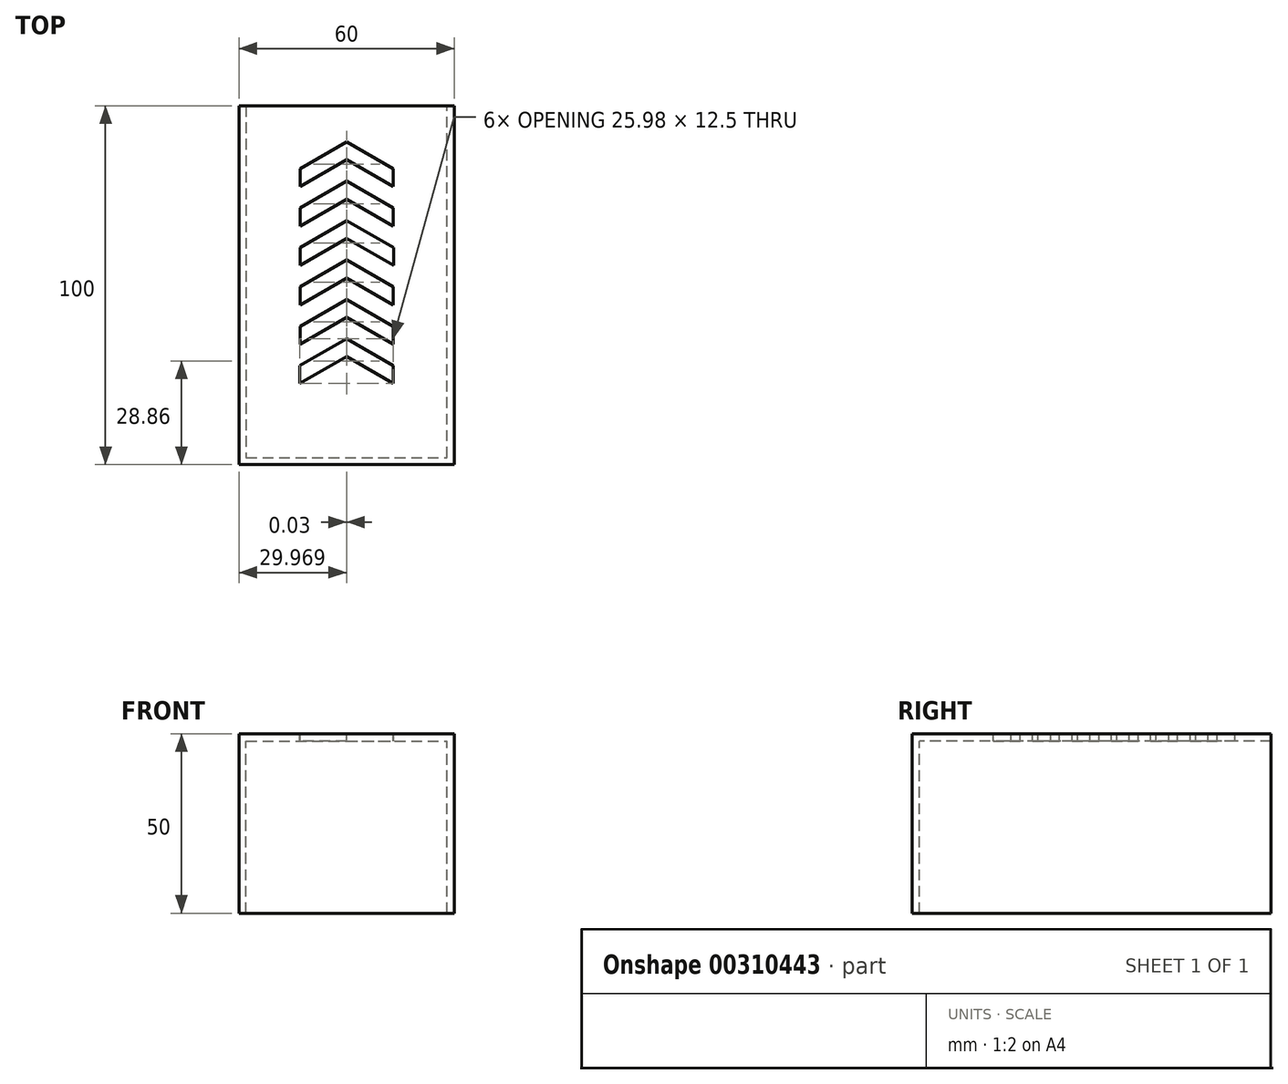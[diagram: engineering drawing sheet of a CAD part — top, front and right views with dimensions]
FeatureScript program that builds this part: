
annotation { "Feature Type Name" : "Feature", "Feature Type Description" : "" }
export const myFeature = defineFeature(function(context is Context, id is Id, definition is map)
    precondition{}
    {
        {
            var Q0;
            Q0=qCreatedBy(makeId("Top.planeOp"),FACE);
            var sketch = newSketch(context, id + "F0", { "sketchPlane" : qUnion([Q0])});
            skLineSegment(sketch, "E0", {"start": v(0, 0) * mm, "end": v(-30, 0) * mm});
            skLineSegment(sketch, "E1", {"start": v(-30, 0) * mm, "end": v(-30, -100) * mm});
            skLineSegment(sketch, "E2", {"start": v(-30, -100) * mm, "end": v(30, -100) * mm});
            skLineSegment(sketch, "E3", {"start": v(30, -100) * mm, "end": v(30, 0) * mm});
            skLineSegment(sketch, "E4", {"start": v(30, 0) * mm, "end": v(0, 0) * mm});
            skSolve(sketch);
        }
        {
            var Q0;
            Q0=makeQuery(id+"F0.imprint","IMPRINT",FACE,{"disambiguationData":[TD([[makeQuery(id+"F0.imprint","IMPRINT",EDGE,{"derivedFrom":sQuery(id+"F0.wireOp",EDGE,"E0")}),1.0]])]});
            extrude(context, id + "F1", {"entities" : qUnion([Q0]), "oppositeDirection" : true, "depth" : 50 * mm});
        }
        {
            var Q0;
            Q0=makeQuery(id+"F1.opExtrude","CAP_FACE",FACE,{"disambiguationData":[OSD([sQuery(id+"F0.wireOp",EDGE,"E0"),sQuery(id+"F0.wireOp",EDGE,"E1"),sQuery(id+"F0.wireOp",EDGE,"E2"),sQuery(id+"F0.wireOp",EDGE,"E3"),sQuery(id+"F0.wireOp",EDGE,"E4")])],"isStart":false});
            shell(context, id + "F2", {"entities" : qUnion([Q0]), "thickness" : 2 * mm});
        }
        {
            var Q0;
            Q0=makeQuery(id+"F1.opExtrude","CAP_FACE",FACE,{"disambiguationData":[OSD([sQuery(id+"F0.wireOp",EDGE,"E0"),sQuery(id+"F0.wireOp",EDGE,"E1"),sQuery(id+"F0.wireOp",EDGE,"E2"),sQuery(id+"F0.wireOp",EDGE,"E3"),sQuery(id+"F0.wireOp",EDGE,"E4")])],"isStart":true});
            var sketch = newSketch(context, id + "F3", { "sketchPlane" : qUnion([Q0])});
            skLineSegment(sketch, "E5", {"start": v(0, 0) * mm, "end": v(0, -10) * mm});
            skLineSegment(sketch, "E6", {"start": v(0, -10) * mm, "end": v(-13, -17.5) * mm});
            skLineSegment(sketch, "E7", {"start": v(-13, -17.5) * mm, "end": v(-13, -22.5) * mm});
            skLineSegment(sketch, "E8", {"start": v(-13, -22.5) * mm, "end": v(0, -15) * mm});
            skLineSegment(sketch, "E9", {"start": v(0, -10) * mm, "end": v(13, -17.5) * mm});
            skLineSegment(sketch, "E10", {"start": v(13, -17.5) * mm, "end": v(13, -22.5) * mm});
            skLineSegment(sketch, "E11", {"start": v(0, -15) * mm, "end": v(13, -22.5) * mm});
            skLineSegment(sketch, "E12", {"start": v(0, -15) * mm, "end": v(0, -21) * mm});
            skLineSegment(sketch, "E13", {"start": v(0, -21) * mm, "end": v(-13, -28.5) * mm});
            skLineSegment(sketch, "E14", {"start": v(-13, -28.5) * mm, "end": v(-13, -33.5) * mm});
            skLineSegment(sketch, "E15", {"start": v(-13, -33.5) * mm, "end": v(0, -26) * mm});
            skLineSegment(sketch, "E16", {"start": v(0, -21) * mm, "end": v(13, -28.5) * mm});
            skLineSegment(sketch, "E17", {"start": v(13, -28.5) * mm, "end": v(13, -33.5) * mm});
            skLineSegment(sketch, "E18", {"start": v(0, -26) * mm, "end": v(13, -33.5) * mm});
            skLineSegment(sketch, "E19", {"start": v(0, -26) * mm, "end": v(0, -32) * mm});
            skLineSegment(sketch, "E20.1.0.0", {"start": v(0.06, -31.98) * mm, "end": v(-12.93, -39.48) * mm});
            skLineSegment(sketch, "E20.1.0.1", {"start": v(-12.93, -44.48) * mm, "end": v(0.06, -36.98) * mm});
            skLineSegment(sketch, "E20.1.0.2", {"start": v(-12.93, -39.48) * mm, "end": v(-12.93, -44.48) * mm});
            skLineSegment(sketch, "E20.1.0.3", {"start": v(0.06, -31.98) * mm, "end": v(13.05, -39.48) * mm});
            skLineSegment(sketch, "E20.1.0.4", {"start": v(0.06, -36.98) * mm, "end": v(13.05, -44.48) * mm});
            skLineSegment(sketch, "E20.1.0.5", {"start": v(13.05, -39.48) * mm, "end": v(13.05, -44.48) * mm});
            skLineSegment(sketch, "E20.direction1", {"start": v(-13, -17.5) * mm, "end": v(-12.93, -39.48) * mm, "construction": true});
            skLineSegment(sketch, "E21", {"start": v(0.06, -36.98) * mm, "end": v(0.06, -42.98) * mm});
            skLineSegment(sketch, "E22.1.0.0", {"start": v(0.03, -47.95) * mm, "end": v(13.02, -55.45) * mm});
            skLineSegment(sketch, "E22.1.0.1", {"start": v(0.03, -42.95) * mm, "end": v(13.02, -50.45) * mm});
            skLineSegment(sketch, "E22.1.0.2", {"start": v(13.02, -50.45) * mm, "end": v(13.02, -55.45) * mm});
            skLineSegment(sketch, "E22.1.0.3", {"start": v(0.03, -42.95) * mm, "end": v(-12.96, -50.45) * mm});
            skLineSegment(sketch, "E22.1.0.4", {"start": v(-12.96, -50.45) * mm, "end": v(-12.96, -55.45) * mm});
            skLineSegment(sketch, "E22.1.0.5", {"start": v(-12.96, -55.45) * mm, "end": v(0.03, -47.95) * mm});
            skLineSegment(sketch, "E22.2.0.0", {"start": v(0, -58.92) * mm, "end": v(13, -66.42) * mm});
            skLineSegment(sketch, "E22.2.0.1", {"start": v(0, -53.92) * mm, "end": v(13, -61.42) * mm});
            skLineSegment(sketch, "E22.2.0.2", {"start": v(13, -61.42) * mm, "end": v(13, -66.42) * mm});
            skLineSegment(sketch, "E22.2.0.3", {"start": v(0, -53.92) * mm, "end": v(-13, -61.42) * mm});
            skLineSegment(sketch, "E22.2.0.4", {"start": v(-13, -61.42) * mm, "end": v(-13, -66.42) * mm});
            skLineSegment(sketch, "E22.2.0.5", {"start": v(-13, -66.42) * mm, "end": v(0, -58.92) * mm});
            skLineSegment(sketch, "E22.3.0.0", {"start": v(-0.03, -69.89) * mm, "end": v(12.96, -77.39) * mm});
            skLineSegment(sketch, "E22.3.0.1", {"start": v(-0.03, -64.89) * mm, "end": v(12.96, -72.39) * mm});
            skLineSegment(sketch, "E22.3.0.2", {"start": v(12.96, -72.39) * mm, "end": v(12.96, -77.39) * mm});
            skLineSegment(sketch, "E22.3.0.3", {"start": v(-0.03, -64.89) * mm, "end": v(-13.02, -72.39) * mm});
            skLineSegment(sketch, "E22.3.0.4", {"start": v(-13.02, -72.4) * mm, "end": v(-13.02, -77.39) * mm});
            skLineSegment(sketch, "E22.3.0.5", {"start": v(-13.02, -77.39) * mm, "end": v(-0.03, -69.89) * mm});
            skLineSegment(sketch, "E22.direction1", {"start": v(0.06, -36.98) * mm, "end": v(0.03, -47.95) * mm, "construction": true});
            skSolve(sketch);
        }
        {
            var Q0;
            Q0=makeQuery(id+"F3.imprint","IMPRINT",FACE,{"disambiguationData":[TD([[makeQuery(id+"F3.imprint","IMPRINT",EDGE,{"derivedFrom":sQuery(id+"F3.wireOp",EDGE,"E6")}),1.0]])]});
            var Q1;
            Q1=makeQuery(id+"F3.imprint","IMPRINT",FACE,{"disambiguationData":[TD([[makeQuery(id+"F3.imprint","IMPRINT",EDGE,{"derivedFrom":sQuery(id+"F3.wireOp",EDGE,"E13")}),1.0]])]});
            var Q2;
            Q2=makeQuery(id+"F3.imprint","IMPRINT",FACE,{"disambiguationData":[TD([[makeQuery(id+"F3.imprint","IMPRINT",EDGE,{"derivedFrom":sQuery(id+"F3.wireOp",EDGE,"E20.1.0.0")}),1.0]])]});
            var Q3;
            Q3=makeQuery(id+"F3.imprint","IMPRINT",FACE,{"disambiguationData":[TD([[makeQuery(id+"F3.imprint","IMPRINT",EDGE,{"derivedFrom":sQuery(id+"F3.wireOp",EDGE,"E22.1.0.0")}),1.0]])]});
            var Q4;
            Q4=makeQuery(id+"F3.imprint","IMPRINT",FACE,{"disambiguationData":[TD([[makeQuery(id+"F3.imprint","IMPRINT",EDGE,{"derivedFrom":sQuery(id+"F3.wireOp",EDGE,"E22.2.0.0")}),1.0]])]});
            var Q5;
            Q5=makeQuery(id+"F3.imprint","IMPRINT",FACE,{"disambiguationData":[TD([[makeQuery(id+"F3.imprint","IMPRINT",EDGE,{"derivedFrom":sQuery(id+"F3.wireOp",EDGE,"E22.3.0.0")}),1.0]])]});
            extrude(context, id + "F4", {"entities" : qUnion([Q0, Q1, Q2, Q3, Q4, Q5]), "operationType" : NewBodyOperationType.REMOVE, "oppositeDirection" : true, "depth" : 10 * mm});
        }
        {
            var Q0;
            Q0=makeQuery(id+"F1.opExtrude","SWEPT_FACE",FACE,{"disambiguationData":[OSD([sQuery(id+"F0.wireOp",EDGE,"E0"),sQuery(id+"F0.wireOp",EDGE,"E4")])]});
            var sketch = newSketch(context, id + "F5", { "sketchPlane" : qUnion([Q0])});
            skLineSegment(sketch, "E23", {"start": v(0, 0) * mm, "end": v(0, -2) * mm});
            skLineSegment(sketch, "E24", {"start": v(-30, -25) * mm, "end": v(-28, -25) * mm});
            skLineSegment(sketch, "E25", {"start": v(0, -50) * mm, "end": v(0, -48) * mm});
            skPoint(sketch, "E25.endSnap0", {"position": v(0, -50) * mm});
            skLineSegment(sketch, "E26", {"start": v(30, -25) * mm, "end": v(28, -25) * mm});
            skLineSegment(sketch, "E27.bottom", {"start": v(28, -48) * mm, "end": v(-28, -48) * mm});
            skLineSegment(sketch, "E27.top", {"start": v(28, -2) * mm, "end": v(-28, -2) * mm});
            skLineSegment(sketch, "E27.left", {"start": v(28, -48) * mm, "end": v(28, -2) * mm});
            skLineSegment(sketch, "E27.right", {"start": v(-28, -48) * mm, "end": v(-28, -2) * mm});
            skSolve(sketch);
        }
        {
            var Q0;
            {var subQ6=sQuery(id+"F5.wireOp",EDGE,"E27.bottom");var subQ7=makeQuery(id+"F5.imprint","INTERSECT",VERTEX,{"derivedFrom":[sQuery(id+"F5.wireOp",EDGE,"E25"),subQ6]});Q0=makeQuery(id+"F5.imprint","IMPRINT",FACE,{"disambiguationData":[TD([[makeQuery(id+"F5.imprint","IMPRINT",EDGE,{"disambiguationData":[TD([[subQ7,1.0]])],"derivedFrom":subQ6}),-1.0]])]});}
            extrude(context, id + "F6", {"entities" : qUnion([Q0]), "operationType" : NewBodyOperationType.REMOVE, "oppositeDirection" : true, "depth" : 5 * mm});
        }
        {
            var Q0;
            Q0=makeQuery(id+"F1.opExtrude","SWEPT_FACE",FACE,{"disambiguationData":[OSD([sQuery(id+"F0.wireOp",EDGE,"E0"),sQuery(id+"F0.wireOp",EDGE,"E4")])]});
            var sketch = newSketch(context, id + "F7", { "sketchPlane" : qUnion([Q0])});
            skLineSegment(sketch, "E28", {"start": v(-28, -48) * mm, "end": v(-28, -50) * mm});
            skLineSegment(sketch, "E29", {"start": v(-28, -50) * mm, "end": v(28, -50) * mm});
            skLineSegment(sketch, "E30", {"start": v(28, -50) * mm, "end": v(28, -48) * mm});
            skLineSegment(sketch, "E31", {"start": v(28, -48) * mm, "end": v(-28, -48) * mm});
            skSolve(sketch);
        }
        {
            var Q0;
            Q0 = qSketchRegion(id + "F7", true);
            extrude(context, id + "F8", {"entities" : qUnion([Q0]), "operationType" : NewBodyOperationType.REMOVE, "oppositeDirection" : true, "depth" : 25 * mm});
        }
    });
